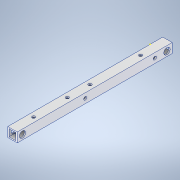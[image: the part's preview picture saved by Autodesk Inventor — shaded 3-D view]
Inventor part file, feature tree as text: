
AUTODESK INVENTOR PART (.ipt)
format: ipt  version: 2020.3 (Build 243373000, 373)  size: 182,272 bytes
history: native  units: mm
features: sketch x9, hole x5, extrude x3, other x1
ambient origin geometry x8: Origin, YZ Plane, XZ Plane, XY Plane, X Axis, Y Axis, Z Axis, Center Point
bodies: Body1 (feature_tree)
feature tree (18):
  other  "ソリッド1"
  extrude  "押し出し1"  Depth=9.0mm
  hole  "穴1"  [1 undecoded]
  hole  "穴2"  [1 undecoded]
  extrude  "押し出し3"  Depth=6.6mm
  hole  "穴4"  [1 undecoded]
  extrude  "押し出し4"  Depth=1.2mm
  hole  "穴5"  [1 undecoded]
  hole  "穴6"  [1 undecoded]
  sketch  "スケッチ11"
  sketch  "スケッチ1"
  sketch  "スケッチ2"
  sketch  "スケッチ3"
  sketch  "スケッチ6"
  sketch  "スケッチ7"
  sketch  "スケッチ8"
  sketch  "スケッチ9"
  sketch  "スケッチ10"
note: 5 required parameter values undecoded (feature->parameter linkage not recoverable at this tier; creation-order binding heuristic only, values carry confidence <= 0.55)
